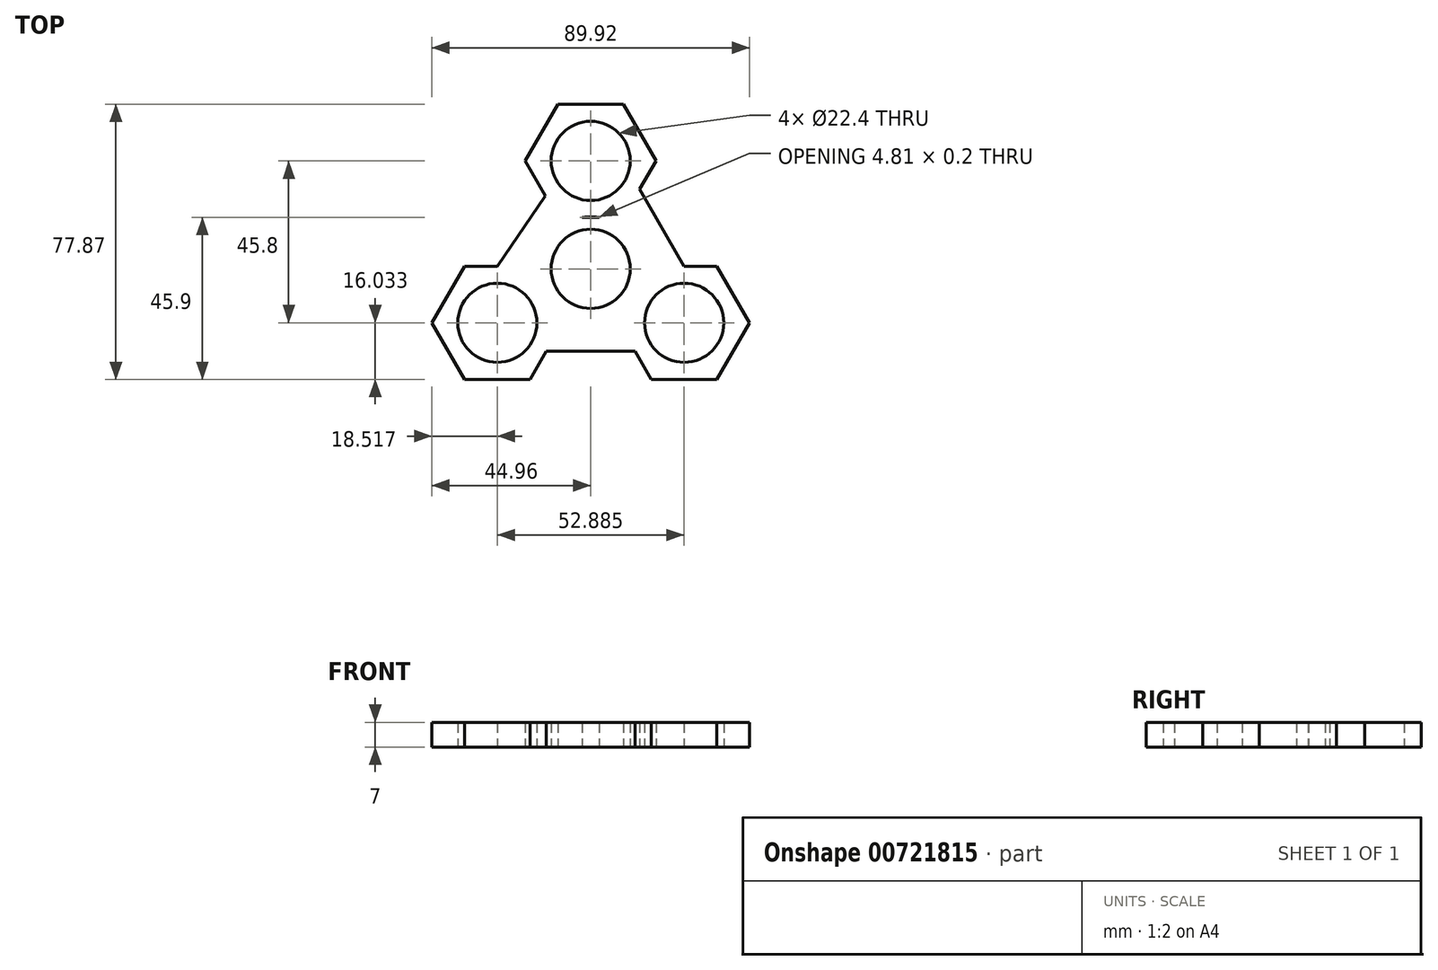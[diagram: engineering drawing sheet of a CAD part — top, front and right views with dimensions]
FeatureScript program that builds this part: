
annotation { "Feature Type Name" : "Feature", "Feature Type Description" : "" }
export const myFeature = defineFeature(function(context is Context, id is Id, definition is map)
    precondition{}
    {
        {
            var Q0;
            Q0=qCreatedBy(makeId("Top.planeOp"),FACE);
            var sketch = newSketch(context, id + "F0", { "sketchPlane" : qUnion([Q0])});
            skPoint(sketch, "E0.0.midPoint", {"position": v(0, 14.7) * mm});
            skPoint(sketch, "E0.cCircle.center.orphan", {"position": v(0, 30.53) * mm});
            skCircle(sketch, "E1", {"center": v(0, 30.53) * mm, "radius": 11.2 * mm});
            skCircle(sketch, "E2", {"center": v(0, 0) * mm, "radius": 11.2 * mm});
            skPoint(sketch, "E3.orphan", {"position": v(11.3, 14.7) * mm});
            skPoint(sketch, "E0.1.start.orphan", {"position": v(-11.3, 14.7) * mm});
            skArc(sketch, "E4.cCircle", {"start": v(-1.74, 14.6) * mm, "mid": v(0, 14.5) * mm, "end": v(1.74, 14.6) * mm, "construction": true});
            skLineSegment(sketch, "E4.0", {"start": v(-9.26, 46.57) * mm, "end": v(9.26, 46.57) * mm});
            skLineSegment(sketch, "E4.1", {"start": v(9.26, 46.57) * mm, "end": v(18.51, 30.53) * mm});
            skLineSegment(sketch, "E4.2", {"start": v(18.51, 30.53) * mm, "end": v(13.88, 22.52) * mm});
            skLineSegment(sketch, "E4.3", {"start": v(2.4, 14.5) * mm, "end": v(-2.4, 14.5) * mm});
            skLineSegment(sketch, "E4.4", {"start": v(-12.84, 20.7) * mm, "end": v(-18.51, 30.53) * mm});
            skLineSegment(sketch, "E4.5", {"start": v(-18.51, 30.53) * mm, "end": v(-9.26, 46.57) * mm});
            skPoint(sketch, "E4.0.midPoint", {"position": v(0, 46.57) * mm});
            skLineSegment(sketch, "E5.1.0", {"start": v(-35.7, 0.77) * mm, "end": v(-26.44, 0.77) * mm});
            skLineSegment(sketch, "E5.1.1", {"start": v(-44.96, -15.27) * mm, "end": v(-35.7, 0.77) * mm});
            skLineSegment(sketch, "E5.1.2", {"start": v(-35.7, -31.3) * mm, "end": v(-44.96, -15.27) * mm});
            skLineSegment(sketch, "E5.1.3", {"start": v(-17.19, -31.3) * mm, "end": v(-35.7, -31.3) * mm});
            skLineSegment(sketch, "E5.1.4", {"start": v(-12.56, -23.28) * mm, "end": v(-17.19, -31.3) * mm});
            skCircle(sketch, "E5.1.6", {"center": v(-26.44, -15.27) * mm, "radius": 11.2 * mm});
            skLineSegment(sketch, "E5.2.0", {"start": v(17.19, -31.3) * mm, "end": v(12.56, -23.28) * mm});
            skLineSegment(sketch, "E5.2.1", {"start": v(35.7, -31.3) * mm, "end": v(17.19, -31.3) * mm});
            skLineSegment(sketch, "E5.2.2", {"start": v(44.96, -15.27) * mm, "end": v(35.7, -31.3) * mm});
            skLineSegment(sketch, "E5.2.3", {"start": v(35.7, 0.77) * mm, "end": v(44.96, -15.27) * mm});
            skLineSegment(sketch, "E5.2.4", {"start": v(26.44, 0.77) * mm, "end": v(35.7, 0.77) * mm});
            skCircle(sketch, "E5.2.6", {"center": v(26.44, -15.27) * mm, "radius": 11.2 * mm});
            skFitSpline(sketch, "E6", {"points": [v(-12.84, 20.7) * mm, v(-26.44, 0.77) * mm], "startDerivative": vector(-13.6, -19.94) * mm, "endDerivative": vector(-13.6, -19.94) * mm});
            skFitSpline(sketch, "E7", {"points": [v(13.88, 22.52) * mm, v(26.44, 0.77) * mm], "startDerivative": vector(12.56, -21.75) * mm, "endDerivative": vector(12.56, -21.75) * mm});
            skFitSpline(sketch, "E8", {"points": [v(-12.56, -23.28) * mm, v(12.56, -23.28) * mm], "startDerivative": vector(25.12, 0) * mm, "endDerivative": vector(25.12, 0) * mm});
            skArc(sketch, "E9.trimOffspring", {"start": v(2.4, 14.5) * mm, "mid": v(0, 14.7) * mm, "end": v(-2.4, 14.5) * mm});
            skPoint(sketch, "E5.1.5.end.orphan", {"position": v(-7.93, -15.27) * mm});
            skPoint(sketch, "E10.orphan", {"position": v(-17.19, 0.77) * mm});
            skPoint(sketch, "E11.orphan", {"position": v(7.93, -15.27) * mm});
            skPoint(sketch, "E12.orphan", {"position": v(17.19, 0.77) * mm});
            skPoint(sketch, "E13.orphan", {"position": v(-9.26, 14.5) * mm});
            skPoint(sketch, "E14.orphan", {"position": v(9.26, 14.5) * mm});
            skSolve(sketch);
        }
        {
            var Q0;
            Q0=makeQuery(id+"F0.imprint","IMPRINT",FACE,{"disambiguationData":[TD([[makeQuery(id+"F0.imprint","IMPRINT",EDGE,{"derivedFrom":sQuery(id+"F0.wireOp",EDGE,"E1")}),-1.0]])]});
            extrude(context, id + "F1", {"entities" : qUnion([Q0]), "depth" : 7 * mm, "offsetDistance" : 25 * mm});
        }
    });
